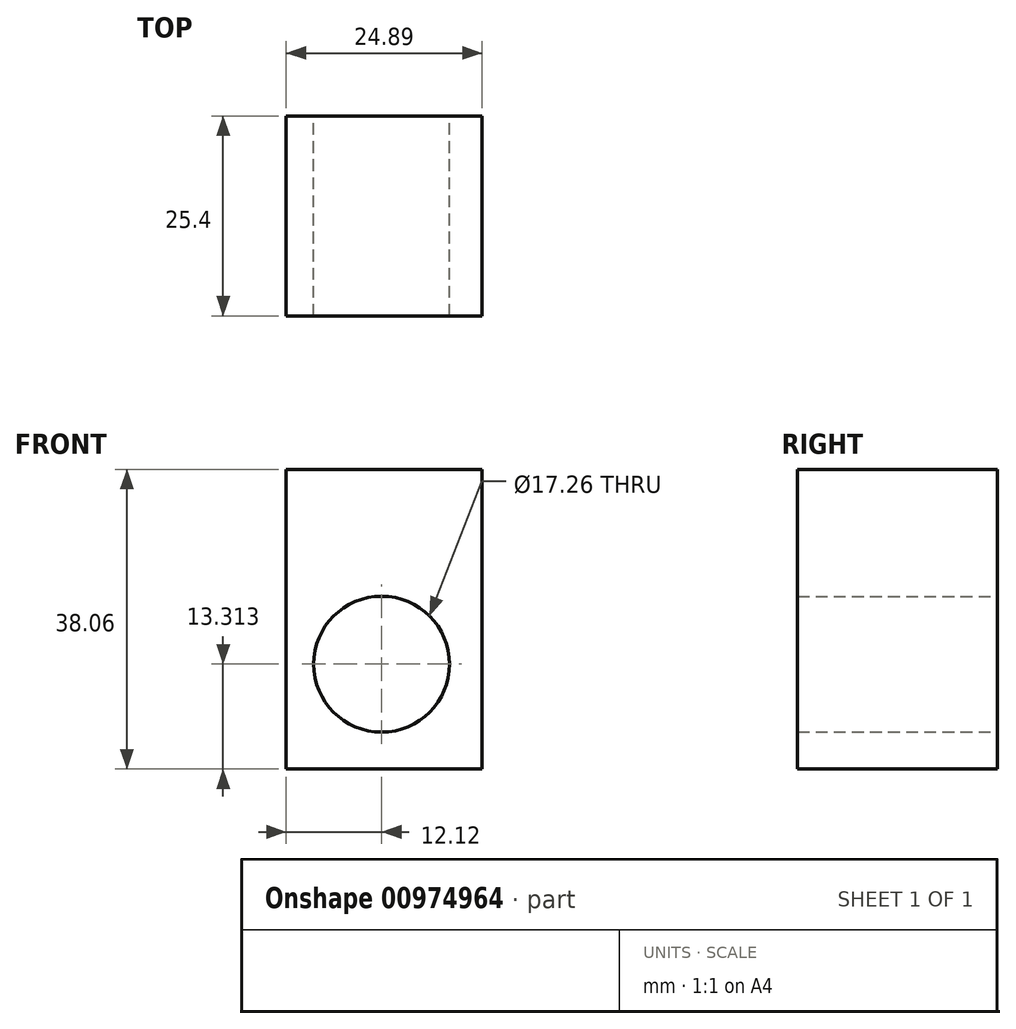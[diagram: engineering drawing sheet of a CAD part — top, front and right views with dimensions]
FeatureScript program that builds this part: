
annotation { "Feature Type Name" : "Feature", "Feature Type Description" : "" }
export const myFeature = defineFeature(function(context is Context, id is Id, definition is map)
    precondition{}
    {
        {
            var Q0;
            Q0=qCreatedBy(makeId("Front.planeOp"),FACE);
            var sketch = newSketch(context, id + "F0", { "sketchPlane" : qUnion([Q0])});
            skLineSegment(sketch, "E0.bottom", {"start": v(-12.12, -4.07) * mm, "end": v(12.77, -4.07) * mm});
            skLineSegment(sketch, "E0.top", {"start": v(-12.12, -42.13) * mm, "end": v(12.77, -42.13) * mm});
            skLineSegment(sketch, "E0.left", {"start": v(-12.12, -4.07) * mm, "end": v(-12.12, -42.13) * mm});
            skLineSegment(sketch, "E0.right", {"start": v(12.77, -4.07) * mm, "end": v(12.77, -42.13) * mm});
            skCircle(sketch, "E1", {"center": v(0, -28.82) * mm, "radius": 8.63 * mm});
            skSolve(sketch);
        }
        {
            var Q0;
            Q0=makeQuery(id+"F0.imprint","IMPRINT",FACE,{"disambiguationData":[TD([[makeQuery(id+"F0.imprint","IMPRINT",EDGE,{"derivedFrom":sQuery(id+"F0.wireOp",EDGE,"E0.bottom")}),-1.0]])]});
            extrude(context, id + "F1", {"entities" : qUnion([Q0]), "depth" : 25.4 * mm, "offsetDistance" : 25.4 * mm});
        }
    });
